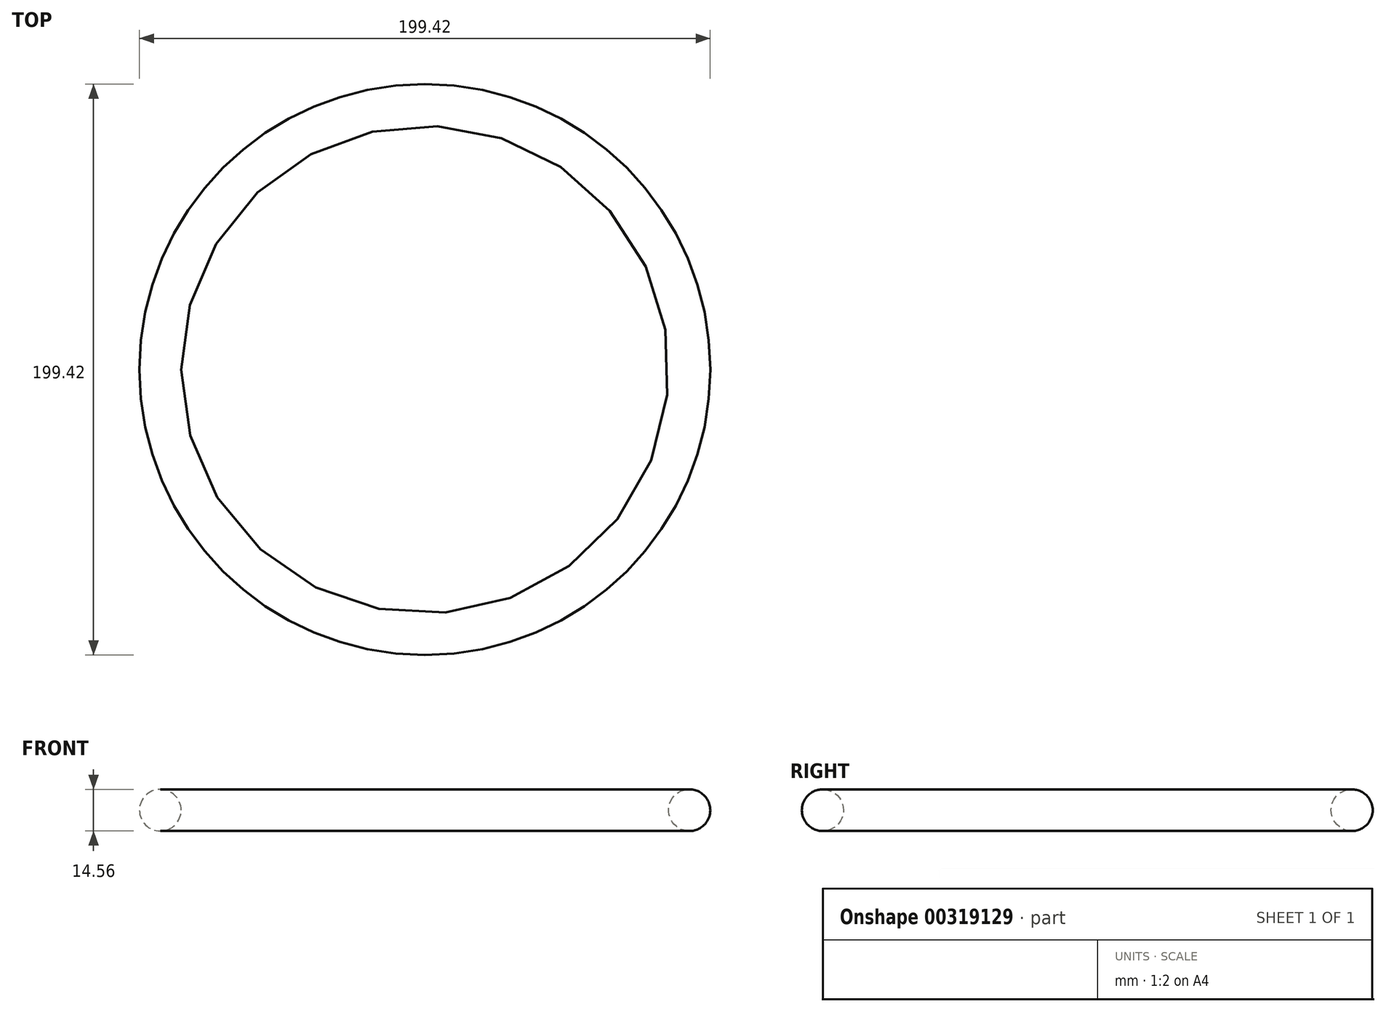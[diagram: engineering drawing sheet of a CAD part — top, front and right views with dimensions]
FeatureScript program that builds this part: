
annotation { "Feature Type Name" : "Feature", "Feature Type Description" : "" }
export const myFeature = defineFeature(function(context is Context, id is Id, definition is map)
    precondition{}
    {
        {
            var Q0;
            Q0=qCreatedBy(makeId("Top.planeOp"),FACE);
            var sketch = newSketch(context, id + "F0", { "sketchPlane" : qUnion([Q0])});
            skCircle(sketch, "E0", {"center": v(0, 0) * mm, "radius": 76.2 * mm});
            skSolve(sketch);
        }
        {
            var Q0;
            Q0=qCreatedBy(makeId("Right.planeOp"),FACE);
            var sketch = newSketch(context, id + "F1", { "sketchPlane" : qUnion([Q0])});
            skCircle(sketch, "E1", {"center": v(-92.44, 0) * mm, "radius": 7.28 * mm});
            skSolve(sketch);
        }
        {
            var Q0;
            Q0=makeQuery(id+"F1.imprint","IMPRINT",FACE,{"disambiguationData":[TD([[makeQuery(id+"F1.imprint","IMPRINT",EDGE,{"derivedFrom":sQuery(id+"F1.wireOp",EDGE,"E1")}),1.0]])]});
            var Q1;
            Q1=sQuery(id+"F0.wireOp",EDGE,"E0");
            revolve(context, id + "F2", {"entities" : qUnion([Q0]), "axis" : qUnion([Q1]), "revolveType" : RevolveType.FULL});
        }
        {
            var Q0;
            Q0=qCreatedBy(makeId("Top.planeOp"),FACE);
            var sketch = newSketch(context, id + "F3", { "sketchPlane" : qUnion([Q0])});
            skCircle(sketch, "E2", {"center": v(0, 0) * mm, "radius": 76.2 * mm});
            skCircle(sketch, "E3", {"center": v(10.66, -75.45) * mm, "radius": 76.2 * mm});
            skCircle(sketch, "E4", {"center": v(70.67, -28.5) * mm, "radius": 76.2 * mm});
            skCircle(sketch, "E5", {"center": v(60.01, 46.96) * mm, "radius": 76.2 * mm});
            skCircle(sketch, "E6", {"center": v(-10.66, 75.45) * mm, "radius": 76.2 * mm});
            skCircle(sketch, "E7", {"center": v(-70.67, 28.5) * mm, "radius": 76.2 * mm});
            skCircle(sketch, "E8", {"center": v(-60.01, -46.96) * mm, "radius": 76.2 * mm});
            skSolve(sketch);
        }
    });
